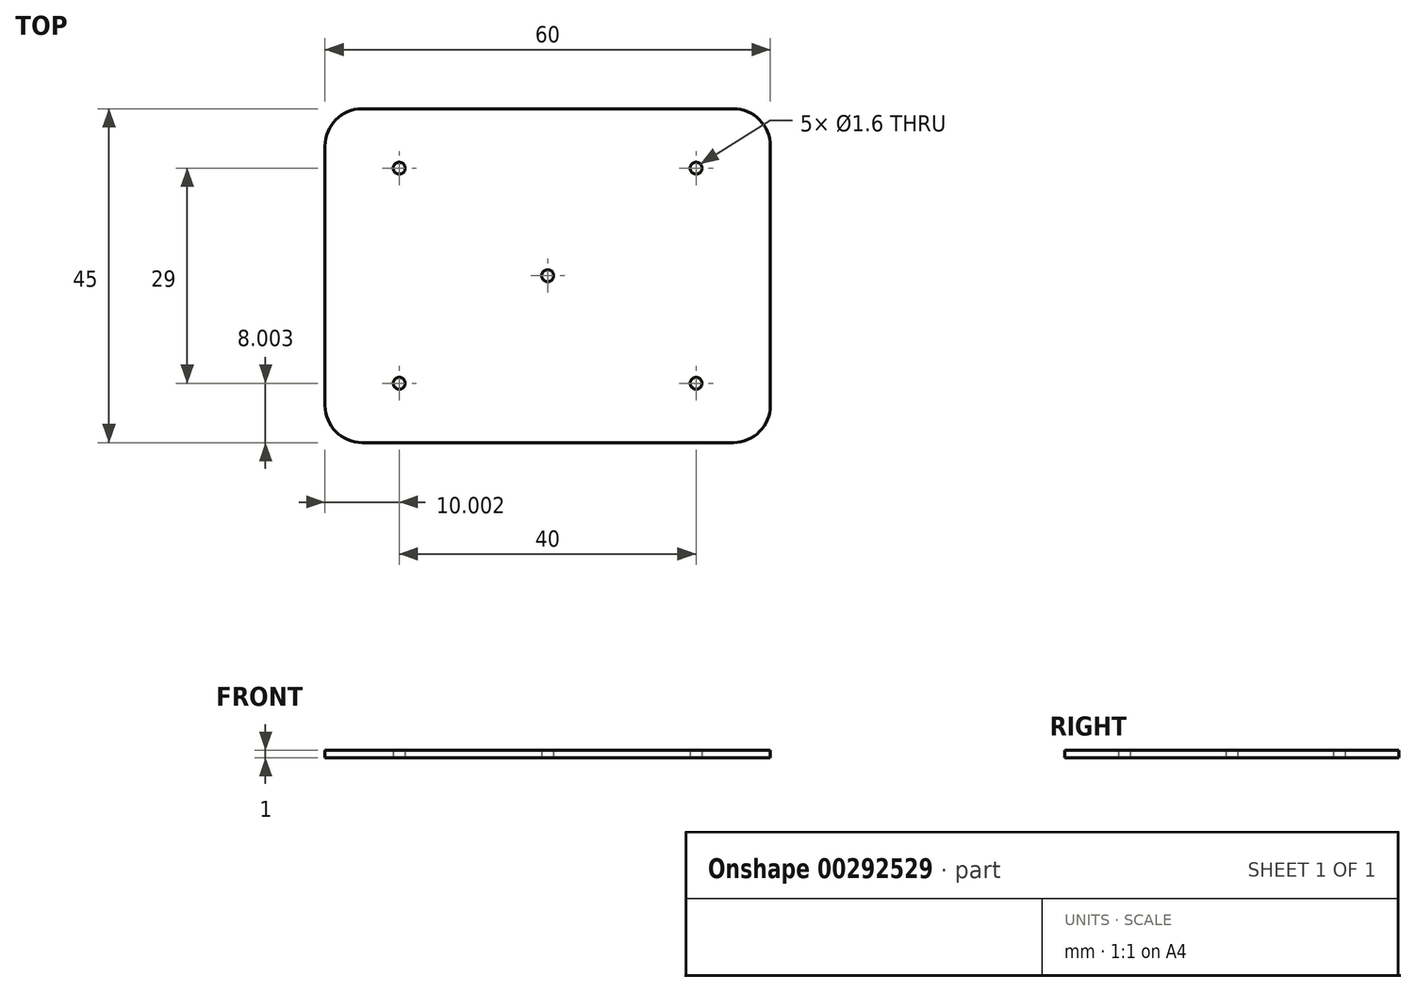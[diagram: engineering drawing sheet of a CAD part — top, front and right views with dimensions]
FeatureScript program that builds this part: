
annotation { "Feature Type Name" : "Feature", "Feature Type Description" : "" }
export const myFeature = defineFeature(function(context is Context, id is Id, definition is map)
    precondition{}
    {
        {
            var Q0;
            Q0=qCreatedBy(makeId("Top.planeOp"),FACE);
            var sketch = newSketch(context, id + "F0", { "sketchPlane" : qUnion([Q0])});
            skLineSegment(sketch, "E0.bottom", {"start": v(-25.22, 21.8) * mm, "end": v(24.78, 21.8) * mm});
            skLineSegment(sketch, "E0.top", {"start": v(-25.22, -23.2) * mm, "end": v(24.78, -23.2) * mm});
            skLineSegment(sketch, "E0.left", {"start": v(-30.22, 16.8) * mm, "end": v(-30.22, -18.2) * mm});
            skLineSegment(sketch, "E0.right", {"start": v(29.78, 16.8) * mm, "end": v(29.78, -18.2) * mm});
            skPoint(sketch, "E1.visualSharp", {"position": v(-30.22, 21.8) * mm});
            skArc(sketch, "E1.filletArc", {"start": v(-25.22, 21.8) * mm, "mid": v(-28.75, 20.34) * mm, "end": v(-30.22, 16.8) * mm});
            skPoint(sketch, "E2.visualSharp", {"position": v(-30.22, -23.2) * mm});
            skArc(sketch, "E2.filletArc", {"start": v(-30.22, -18.2) * mm, "mid": v(-28.75, -21.73) * mm, "end": v(-25.22, -23.2) * mm});
            skPoint(sketch, "E3.visualSharp", {"position": v(29.78, -23.2) * mm});
            skArc(sketch, "E3.filletArc", {"start": v(24.78, -23.2) * mm, "mid": v(28.32, -21.73) * mm, "end": v(29.78, -18.2) * mm});
            skPoint(sketch, "E4.visualSharp", {"position": v(29.78, 21.8) * mm});
            skArc(sketch, "E4.filletArc", {"start": v(29.78, 16.8) * mm, "mid": v(28.32, 20.34) * mm, "end": v(24.78, 21.8) * mm});
            skCircle(sketch, "E5", {"center": v(-20.22, 13.8) * mm, "radius": 0.8 * mm});
            skCircle(sketch, "E6", {"center": v(19.78, 13.8) * mm, "radius": 0.8 * mm});
            skCircle(sketch, "E7", {"center": v(19.78, -15.2) * mm, "radius": 0.8 * mm});
            skCircle(sketch, "E8", {"center": v(-20.22, -15.2) * mm, "radius": 0.8 * mm});
            skCircle(sketch, "E9", {"center": v(-0.22, -0.7) * mm, "radius": 0.8 * mm});
            skSolve(sketch);
        }
        {
            var Q0;
            Q0=makeQuery(id+"F0.imprint","IMPRINT",FACE,{"disambiguationData":[TD([[makeQuery(id+"F0.imprint","IMPRINT",EDGE,{"derivedFrom":sQuery(id+"F0.wireOp",EDGE,"E0.bottom")}),-1.0]])]});
            extrude(context, id + "F1", {"entities" : qUnion([Q0]), "depth" : 1 * mm});
        }
    });
